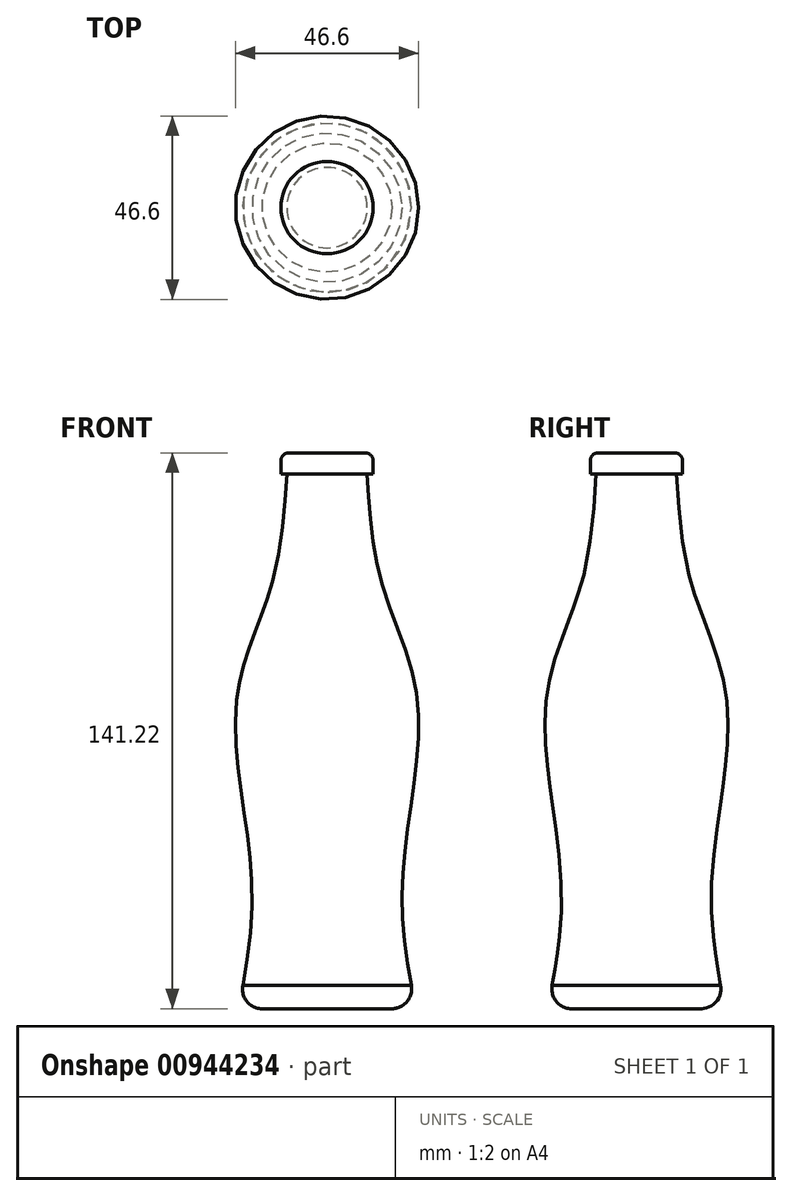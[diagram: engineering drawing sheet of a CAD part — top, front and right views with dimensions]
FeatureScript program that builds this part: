
annotation { "Feature Type Name" : "Feature", "Feature Type Description" : "" }
export const myFeature = defineFeature(function(context is Context, id is Id, definition is map)
    precondition{}
    {
        {
            var Q0;
            Q0=qCreatedBy(makeId("Top.planeOp"),FACE);
            var sketch = newSketch(context, id + "F0", { "sketchPlane" : qUnion([Q0])});
            skCircle(sketch, "E0", {"center": v(0, 0) * mm, "radius": 22.48 * mm});
            skSolve(sketch);
        }
        {
            var Q0;
            Q0=qCreatedBy(makeId("Top.planeOp"),FACE);
            cPlane(context, id + "F1", {"entities" : qUnion([Q0]), "cplaneType" : CPlaneType.OFFSET, "offset" : 26.67 * mm, "width" : 152.4 * mm, "height" : 152.4 * mm});
        }
        {
            var Q0;
            Q0=qCreatedBy(id+"F1.planeOp",FACE);
            var sketch = newSketch(context, id + "F2", { "sketchPlane" : qUnion([Q0])});
            skCircle(sketch, "E1", {"center": v(0, 0) * mm, "radius": 19.02 * mm});
            skSolve(sketch);
        }
        {
            var Q0;
            Q0=qCreatedBy(id+"F1.planeOp",FACE);
            cPlane(context, id + "F3", {"entities" : qUnion([Q0]), "cplaneType" : CPlaneType.OFFSET, "offset" : 27.94 * mm, "width" : 152.4 * mm, "height" : 152.4 * mm});
        }
        {
            var Q0;
            Q0=qCreatedBy(id+"F3.planeOp",FACE);
            cPlane(context, id + "F4", {"entities" : qUnion([Q0]), "cplaneType" : CPlaneType.OFFSET, "offset" : 26.92 * mm, "width" : 152.4 * mm, "height" : 152.4 * mm});
        }
        {
            var Q0;
            Q0=qCreatedBy(id+"F4.planeOp",FACE);
            cPlane(context, id + "F5", {"entities" : qUnion([Q0]), "cplaneType" : CPlaneType.OFFSET, "offset" : 26.92 * mm, "width" : 152.4 * mm, "height" : 152.4 * mm});
        }
        {
            var Q0;
            Q0=qCreatedBy(id+"F5.planeOp",FACE);
            cPlane(context, id + "F6", {"entities" : qUnion([Q0]), "cplaneType" : CPlaneType.OFFSET, "offset" : 27.43 * mm, "width" : 152.4 * mm, "height" : 152.4 * mm});
        }
        {
            var Q0;
            Q0=qCreatedBy(id+"F3.planeOp",FACE);
            var sketch = newSketch(context, id + "F7", { "sketchPlane" : qUnion([Q0])});
            skCircle(sketch, "E2", {"center": v(0, 0) * mm, "radius": 21.73 * mm});
            skSolve(sketch);
        }
        {
            var Q0;
            Q0=qCreatedBy(id+"F4.planeOp",FACE);
            var sketch = newSketch(context, id + "F8", { "sketchPlane" : qUnion([Q0])});
            skCircle(sketch, "E3", {"center": v(0, 0) * mm, "radius": 22.53 * mm});
            skSolve(sketch);
        }
        {
            var Q0;
            Q0=qCreatedBy(id+"F5.planeOp",FACE);
            var sketch = newSketch(context, id + "F9", { "sketchPlane" : qUnion([Q0])});
            skCircle(sketch, "E4", {"center": v(0, 0) * mm, "radius": 13.84 * mm});
            skSolve(sketch);
        }
        {
            var Q0;
            Q0=qCreatedBy(id+"F6.planeOp",FACE);
            var sketch = newSketch(context, id + "F10", { "sketchPlane" : qUnion([Q0])});
            skCircle(sketch, "E5", {"center": v(0, 0) * mm, "radius": 10.21 * mm});
            skSolve(sketch);
        }
        {
            var Q0;
            Q0=makeQuery(id+"F10.imprint","IMPRINT",FACE,{"disambiguationData":[TD([[makeQuery(id+"F10.imprint","IMPRINT",EDGE,{"derivedFrom":sQuery(id+"F10.wireOp",EDGE,"E5")}),1.0]])]});
            var Q1;
            Q1=makeQuery(id+"F9.imprint","IMPRINT",FACE,{"disambiguationData":[TD([[makeQuery(id+"F9.imprint","IMPRINT",EDGE,{"derivedFrom":sQuery(id+"F9.wireOp",EDGE,"E4")}),1.0]])]});
            var Q2;
            Q2=makeQuery(id+"F8.imprint","IMPRINT",FACE,{"disambiguationData":[TD([[makeQuery(id+"F8.imprint","IMPRINT",EDGE,{"derivedFrom":sQuery(id+"F8.wireOp",EDGE,"E3")}),1.0]])]});
            var Q3;
            Q3=makeQuery(id+"F7.imprint","IMPRINT",FACE,{"disambiguationData":[TD([[makeQuery(id+"F7.imprint","IMPRINT",EDGE,{"derivedFrom":sQuery(id+"F7.wireOp",EDGE,"E2")}),1.0]])]});
            var Q4;
            Q4=makeQuery(id+"F2.imprint","IMPRINT",FACE,{"disambiguationData":[TD([[makeQuery(id+"F2.imprint","IMPRINT",EDGE,{"derivedFrom":sQuery(id+"F2.wireOp",EDGE,"E1")}),1.0]])]});
            var Q5;
            Q5=makeQuery(id+"F0.imprint","IMPRINT",FACE,{"disambiguationData":[TD([[makeQuery(id+"F0.imprint","IMPRINT",EDGE,{"derivedFrom":sQuery(id+"F0.wireOp",EDGE,"E0")}),1.0]])]});
            loft(context, id + "F11", {"sheetProfilesArray" : [{ "sheetProfileEntities" : qUnion([Q0]) }, { "sheetProfileEntities" : qUnion([Q1]) }, { "sheetProfileEntities" : qUnion([Q2]) }, { "sheetProfileEntities" : qUnion([Q3]) }, { "sheetProfileEntities" : qUnion([Q4]) }, { "sheetProfileEntities" : qUnion([Q5]) }]});
        }
        {
            var Q0;
            Q0=qCreatedBy(id+"F6.planeOp",FACE);
            var sketch = newSketch(context, id + "F12", { "sketchPlane" : qUnion([Q0])});
            skCircle(sketch, "E6", {"center": v(0, 0) * mm, "radius": 11.72 * mm});
            skSolve(sketch);
        }
        {
            var Q0;
            Q0 = qSketchRegion(id + "F12", true);
            extrude(context, id + "F13", {"entities" : qUnion([Q0]), "operationType" : NewBodyOperationType.ADD, "depth" : 5.33 * mm, "offsetDistance" : 25.4 * mm});
        }
        {
            var Q0;
            Q0=makeQuery(id+"F13.opExtrude","CAP_EDGE",EDGE,{"disambiguationData":[OSD([sQuery(id+"F12.wireOp",EDGE,"E6")])],"isStart":false});
            fillet(context, id + "F14", {"entities" : qUnion([Q0]), "radius" : 2 * mm, "tangentPropagation" : true, "allowEdgeOverflow" : false});
        }
        {
            var Q0;
            Q0=makeQuery(id+"F11.opLoft","MID_CAP_EDGE",EDGE,{"disambiguationData":[OSD([sQuery(id+"F0.wireOp",EDGE,"E0")])],"capPos":5.0});
            fillet(context, id + "F15", {"entities" : qUnion([Q0]), "radius" : 5 * mm, "tangentPropagation" : true, "allowEdgeOverflow" : false});
        }
    });
